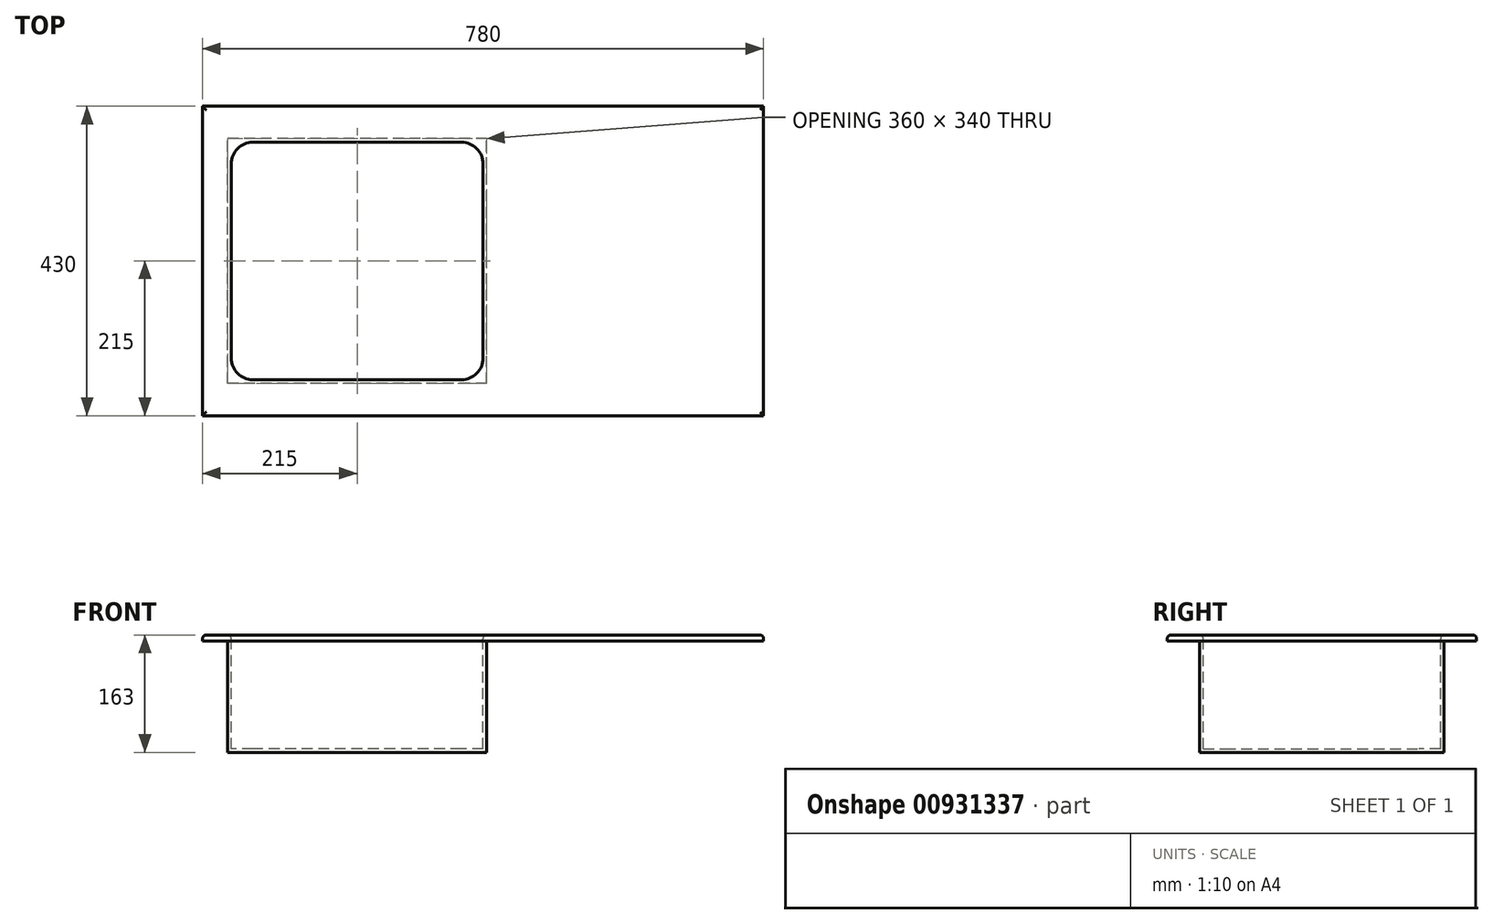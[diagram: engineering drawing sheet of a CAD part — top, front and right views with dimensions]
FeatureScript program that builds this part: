
annotation { "Feature Type Name" : "Feature", "Feature Type Description" : "" }
export const myFeature = defineFeature(function(context is Context, id is Id, definition is map)
    precondition{}
    {
        {
            var Q0;
            Q0=qCreatedBy(makeId("Top.planeOp"),FACE);
            var sketch = newSketch(context, id + "F0", { "sketchPlane" : qUnion([Q0])});
            skLineSegment(sketch, "E0.bottom", {"start": v(390, 215) * mm, "end": v(-390, 215) * mm});
            skLineSegment(sketch, "E0.top", {"start": v(390, -215) * mm, "end": v(-390, -215) * mm});
            skLineSegment(sketch, "E0.left", {"start": v(390, 215) * mm, "end": v(390, -215) * mm});
            skLineSegment(sketch, "E0.right", {"start": v(-390, 215) * mm, "end": v(-390, -215) * mm});
            skPoint(sketch, "E0.middle", {"position": v(0, 0) * mm});
            skSolve(sketch);
        }
        {
            var Q0;
            Q0=makeQuery(id+"F0.imprint","IMPRINT",FACE,{"disambiguationData":[TD([[makeQuery(id+"F0.imprint","IMPRINT",EDGE,{"derivedFrom":sQuery(id+"F0.wireOp",EDGE,"E0.bottom")}),1.0]])]});
            extrude(context, id + "F1", {"entities" : qUnion([Q0]), "depth" : 8 * mm, "offsetDistance" : 25 * mm});
        }
        {
            var Q0;
            Q0=makeQuery(id+"F1.opExtrude","CAP_FACE",FACE,{"disambiguationData":[OSD([sQuery(id+"F0.wireOp",EDGE,"E0.bottom"),sQuery(id+"F0.wireOp",EDGE,"E0.top"),sQuery(id+"F0.wireOp",EDGE,"E0.left"),sQuery(id+"F0.wireOp",EDGE,"E0.right")])],"isStart":false});
            var sketch = newSketch(context, id + "F2", { "sketchPlane" : qUnion([Q0])});
            skSolve(sketch);
        }
        {
            var Q0;
            Q0=makeQuery(id+"F2.imprint","IMPRINT",FACE,{"disambiguationData":[TD([[makeQuery(id+"F2.imprint","IMPRINT",EDGE,{"derivedFrom":makeQuery(id+"F1.opExtrude","CAP_EDGE",EDGE,{"disambiguationData":[OSD([sQuery(id+"F0.wireOp",EDGE,"E0.bottom")])],"isStart":false})}),1.0]])]});
            var sketch = newSketch(context, id + "F3", { "sketchPlane" : qUnion([Q0])});
            skLineSegment(sketch, "E1.bottom", {"start": v(0, -165) * mm, "end": v(-350, -165) * mm});
            skLineSegment(sketch, "E1.top", {"start": v(0, 165) * mm, "end": v(-350, 165) * mm});
            skLineSegment(sketch, "E1.left", {"start": v(0, -165) * mm, "end": v(0, 165) * mm});
            skLineSegment(sketch, "E1.right", {"start": v(-350, -165) * mm, "end": v(-350, 165) * mm});
            skPoint(sketch, "E1.middle", {"position": v(-175, 0) * mm});
            skSolve(sketch);
        }
        {
            var Q0;
            Q0=makeQuery(id+"F3.imprint","IMPRINT",FACE,{"disambiguationData":[TD([[makeQuery(id+"F3.imprint","IMPRINT",EDGE,{"derivedFrom":sQuery(id+"F3.wireOp",EDGE,"E1.bottom")}),-1.0]])]});
            extrude(context, id + "F4", {"entities" : qUnion([Q0]), "operationType" : NewBodyOperationType.REMOVE, "oppositeDirection" : true, "depth" : 25 * mm, "offsetDistance" : 25 * mm});
        }
        {
            var Q0;
            Q0=makeQuery(id+"F1.opExtrude","CAP_FACE",FACE,{"disambiguationData":[OSD([sQuery(id+"F0.wireOp",EDGE,"E0.bottom"),sQuery(id+"F0.wireOp",EDGE,"E0.top"),sQuery(id+"F0.wireOp",EDGE,"E0.left"),sQuery(id+"F0.wireOp",EDGE,"E0.right")])],"isStart":true});
            var sketch = newSketch(context, id + "F5", { "sketchPlane" : qUnion([Q0])});
            skLineSegment(sketch, "E2.0", {"start": v(0, 165) * mm, "end": v(-350, 165) * mm});
            skLineSegment(sketch, "E3.0", {"start": v(-350, 165) * mm, "end": v(-350, -165) * mm});
            skLineSegment(sketch, "E4.0", {"start": v(0, 165) * mm, "end": v(0, -165) * mm});
            skLineSegment(sketch, "E5.0", {"start": v(0, -165) * mm, "end": v(-350, -165) * mm});
            skLineSegment(sketch, "E6.0", {"start": v(5, 170) * mm, "end": v(-355, 170) * mm});
            skLineSegment(sketch, "E6.1", {"start": v(5, 170) * mm, "end": v(5, -170) * mm});
            skLineSegment(sketch, "E6.2", {"start": v(5, -170) * mm, "end": v(-355, -170) * mm});
            skLineSegment(sketch, "E6.3", {"start": v(-355, 170) * mm, "end": v(-355, -170) * mm});
            skSolve(sketch);
        }
        {
            var Q0;
            Q0=makeQuery(id+"F5.imprint","IMPRINT",FACE,{"disambiguationData":[TD([[makeQuery(id+"F5.imprint","IMPRINT",EDGE,{"derivedFrom":sQuery(id+"F5.wireOp",EDGE,"E2.0")}),-1.0]])]});
            extrude(context, id + "F6", {"entities" : qUnion([Q0]), "operationType" : NewBodyOperationType.ADD, "depth" : 150 * mm, "offsetDistance" : 25 * mm});
        }
        {
            var Q0;
            Q0=makeQuery(id+"F6.opExtrude","CAP_FACE",FACE,{"disambiguationData":[OSD([sQuery(id+"F5.wireOp",EDGE,"E2.0"),sQuery(id+"F5.wireOp",EDGE,"E3.0"),sQuery(id+"F5.wireOp",EDGE,"E4.0"),sQuery(id+"F5.wireOp",EDGE,"E5.0"),sQuery(id+"F5.wireOp",EDGE,"E6.0"),sQuery(id+"F5.wireOp",EDGE,"E6.1"),sQuery(id+"F5.wireOp",EDGE,"E6.2"),sQuery(id+"F5.wireOp",EDGE,"E6.3")])],"isStart":false});
            var sketch = newSketch(context, id + "F7", { "sketchPlane" : qUnion([Q0])});
            skLineSegment(sketch, "E7.0", {"start": v(-355, 170) * mm, "end": v(-355, -170) * mm});
            skLineSegment(sketch, "E8.0", {"start": v(5, 170) * mm, "end": v(-355, 170) * mm});
            skLineSegment(sketch, "E9.0", {"start": v(5, -170) * mm, "end": v(-355, -170) * mm});
            skLineSegment(sketch, "E10.0", {"start": v(5, 170) * mm, "end": v(5, -170) * mm});
            skSolve(sketch);
        }
        {
            var Q0;
            Q0=makeQuery(id+"F7.imprint","IMPRINT",FACE,{"disambiguationData":[TD([[makeQuery(id+"F7.imprint","IMPRINT",EDGE,{"derivedFrom":sQuery(id+"F7.wireOp",EDGE,"E7.0")}),1.0]])]});
            var Q1;
            Q1=makeQuery(id+"F7.imprint","IMPRINT",FACE,{"disambiguationData":[TD([[makeQuery(id+"F7.imprint","IMPRINT",EDGE,{"derivedFrom":makeQuery(id+"F6.opExtrude","CAP_EDGE",EDGE,{"disambiguationData":[OSD([sQuery(id+"F5.wireOp",EDGE,"E2.0")])],"isStart":false})}),1.0]])]});
            extrude(context, id + "F8", {"entities" : qUnion([Q0, Q1]), "operationType" : NewBodyOperationType.ADD, "depth" : 5 * mm, "offsetDistance" : 25 * mm});
        }
        {
            var Q0;
            Q0=makeQuery(id+"F6.opExtrude","CAP_EDGE",EDGE,{"disambiguationData":[OSD([sQuery(id+"F5.wireOp",EDGE,"E5.0")])],"isStart":false});
            var Q1;
            Q1=makeQuery(id+"F6.opExtrude","CAP_EDGE",EDGE,{"disambiguationData":[OSD([sQuery(id+"F5.wireOp",EDGE,"E4.0")])],"isStart":false});
            var Q2;
            Q2=makeQuery(id+"F6.opExtrude","CAP_EDGE",EDGE,{"disambiguationData":[OSD([sQuery(id+"F5.wireOp",EDGE,"E2.0")])],"isStart":false});
            var Q3;
            Q3=makeQuery(id+"F6.boolean.opBoolean","MERGE",EDGE,{"derivedFrom":[makeQuery(id+"F4.boolean.opBoolean","COPY",EDGE,{"derivedFrom":makeQuery(id+"F4.opExtrude","SWEPT_EDGE",EDGE,{"disambiguationData":[OSD([sQuery(id+"F3.wireOp",EDGE,"E1.bottom"),sQuery(id+"F3.wireOp",EDGE,"E1.left")])]})}),makeQuery(id+"F6.opExtrude","SWEPT_EDGE",EDGE,{"disambiguationData":[OSD([sQuery(id+"F5.wireOp",EDGE,"E2.0"),sQuery(id+"F5.wireOp",EDGE,"E4.0")])]})]});
            var Q4;
            Q4=makeQuery(id+"F6.boolean.opBoolean","MERGE",EDGE,{"derivedFrom":[makeQuery(id+"F4.boolean.opBoolean","COPY",EDGE,{"derivedFrom":makeQuery(id+"F4.opExtrude","SWEPT_EDGE",EDGE,{"disambiguationData":[OSD([sQuery(id+"F3.wireOp",EDGE,"E1.top"),sQuery(id+"F3.wireOp",EDGE,"E1.left")])]})}),makeQuery(id+"F6.opExtrude","SWEPT_EDGE",EDGE,{"disambiguationData":[OSD([sQuery(id+"F5.wireOp",EDGE,"E4.0"),sQuery(id+"F5.wireOp",EDGE,"E5.0")])]})]});
            var Q5;
            Q5=makeQuery(id+"F6.boolean.opBoolean","MERGE",EDGE,{"derivedFrom":[makeQuery(id+"F4.boolean.opBoolean","COPY",EDGE,{"derivedFrom":makeQuery(id+"F4.opExtrude","SWEPT_EDGE",EDGE,{"disambiguationData":[OSD([sQuery(id+"F3.wireOp",EDGE,"E1.top"),sQuery(id+"F3.wireOp",EDGE,"E1.right")])]})}),makeQuery(id+"F6.opExtrude","SWEPT_EDGE",EDGE,{"disambiguationData":[OSD([sQuery(id+"F5.wireOp",EDGE,"E3.0"),sQuery(id+"F5.wireOp",EDGE,"E5.0")])]})]});
            var Q6;
            Q6=makeQuery(id+"F6.opExtrude","CAP_EDGE",EDGE,{"disambiguationData":[OSD([sQuery(id+"F5.wireOp",EDGE,"E3.0")])],"isStart":false});
            var Q7;
            Q7=makeQuery(id+"F6.boolean.opBoolean","MERGE",EDGE,{"derivedFrom":[makeQuery(id+"F4.boolean.opBoolean","COPY",EDGE,{"derivedFrom":makeQuery(id+"F4.opExtrude","SWEPT_EDGE",EDGE,{"disambiguationData":[OSD([sQuery(id+"F3.wireOp",EDGE,"E1.bottom"),sQuery(id+"F3.wireOp",EDGE,"E1.right")])]})}),makeQuery(id+"F6.opExtrude","SWEPT_EDGE",EDGE,{"disambiguationData":[OSD([sQuery(id+"F5.wireOp",EDGE,"E2.0"),sQuery(id+"F5.wireOp",EDGE,"E3.0")])]})]});
            fillet(context, id + "F9", {"entities" : qUnion([Q0, Q1, Q2, Q3, Q4, Q5, Q6, Q7]), "radius" : 30 * mm, "tangentPropagation" : true, "allowEdgeOverflow" : false});
        }
        {
            var Q0;
            Q0=makeQuery(id+"F1.opExtrude","CAP_EDGE",EDGE,{"disambiguationData":[OSD([sQuery(id+"F0.wireOp",EDGE,"E0.right")])],"isStart":false});
            var Q1;
            Q1=makeQuery(id+"F1.opExtrude","CAP_FACE",FACE,{"disambiguationData":[OSD([sQuery(id+"F0.wireOp",EDGE,"E0.bottom"),sQuery(id+"F0.wireOp",EDGE,"E0.top"),sQuery(id+"F0.wireOp",EDGE,"E0.left"),sQuery(id+"F0.wireOp",EDGE,"E0.right")])],"isStart":false});
            fillet(context, id + "F10", {"entities" : qUnion([Q0, Q1]), "radius" : 5 * mm, "tangentPropagation" : true, "allowEdgeOverflow" : false});
        }
    });
